# Revit family: Paver-Assembly-Calarc_Pavers-Stepstone-Small-Ashlar_Pattern-4
name_source: partatom
category: Site
units: mm (PartAtom-declared; Revit-internal decimal feet)

## family parameters
Always vertical = Yes
Cut with Voids When Loaded = No
Part Type = Normal
Round Connector Dimension = Use Diameter
Shared = No
Work Plane-Based = No

## types (7) — shared parameters
Description = Small Ashlar Pattern Guide
Manufacturer = Stepstone, Inc
Manufacturer Fax = 310.217.1424
Model = Small Ashlar Pattern
Product Page URL = http://www.stepstoneinc.com
Revit Object Download Link = http://library.smartbim.com
Subcategory = CalArc Pavers
Surface Finish = Integral
URL = stepstoneinc.com

## per-type parameters (varying)
| type | Paver A Pattern | Paver B Pattern | Paver Block A | Paver Block B | Paver Block B1 | Paver Block C | Paver C Pattern |
| 1800 Color Option 1 | Concrete - Stepstone - Almond1806 | Concrete - Stepstone - Granada1801 | Yes | Yes | Yes | No | Concrete - Stepstone - Granada1801 |
| 1800 Color Option 2 | Concrete - Stepstone - Kona1821 | Concrete - Stepstone - Almond1806 | Yes | Yes | Yes | No | Concrete - Stepstone - Almond1806 |
| 1800 Color Option 3 | Concrete - Stepstone - Granada1801 | Concrete - Stepstone - Porcelain1813 | No | No | Yes | Yes | Concrete - Stepstone - French1804 |
| 1800 Color Option 4 | Concrete - Stepstone - Pebble 1824 | Concrete - Stepstone - Kona1821 | No | No | Yes | Yes | Concrete - Stepstone - Granada1801 |
| 1400 Color Option 1 | Concrete - Stepstone - Kona1421 | Concrete - Stepstone - Granada1401 | No | No | Yes | Yes | Concrete - Stepstone - Caramel1410 |
| 1400 Color Option 2 | Concrete - Stepstone - Cafe1407 | Concrete - Stepstone - Almond1406 | Yes | Yes | No | No | Concrete - Stepstone - Almond1406 |
| 1400 Color Option 3 | Concrete - Stepstone - Brick1416 | Concrete - Stepstone - Almond1406 | Yes | Yes | No | No | Concrete - Stepstone - Almond1406 |

## geometry (parser evidence)
native form markers: Blend x11, Sweep x12
no freeform markers — native parametric forms only
